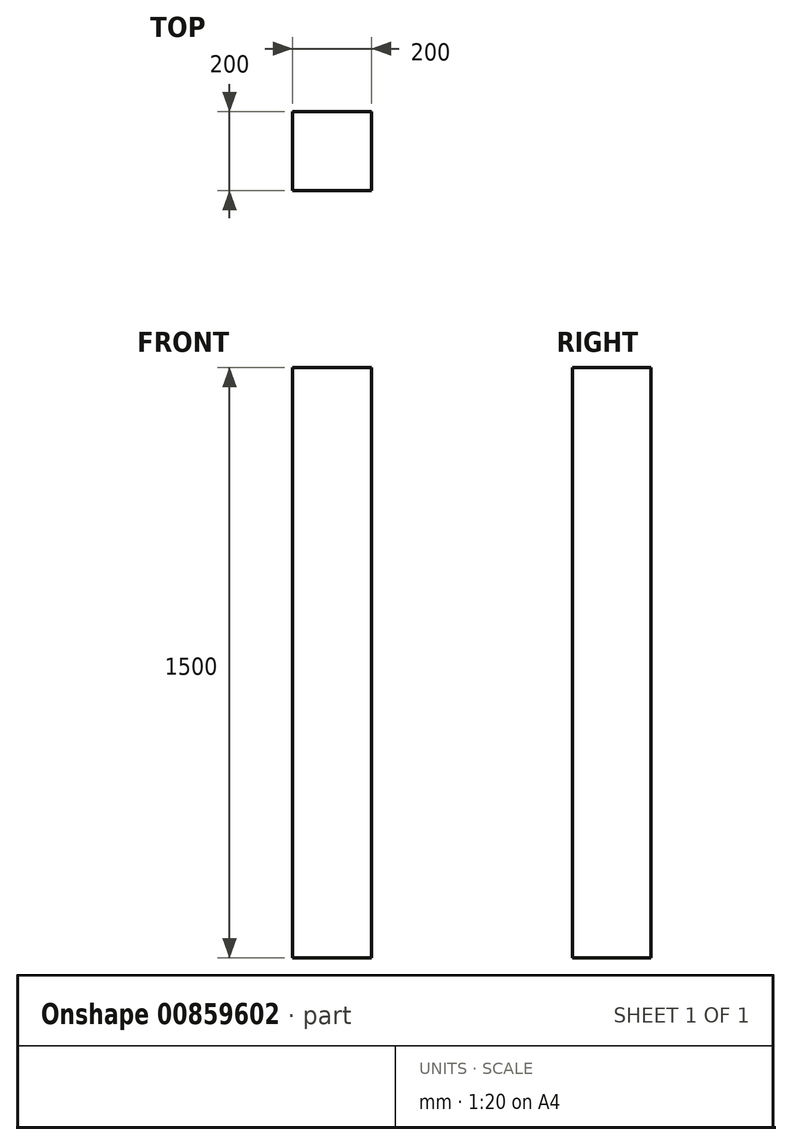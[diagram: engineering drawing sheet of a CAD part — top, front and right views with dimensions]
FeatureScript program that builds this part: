
annotation { "Feature Type Name" : "Feature", "Feature Type Description" : "" }
export const myFeature = defineFeature(function(context is Context, id is Id, definition is map)
    precondition{}
    {
        {
            var Q0;
            Q0=qCreatedBy(makeId("Top.planeOp"),FACE);
            var sketch = newSketch(context, id + "F0", { "sketchPlane" : qUnion([Q0])});
            skLineSegment(sketch, "E0.bottom", {"start": v(-113.92, 101.97) * mm, "end": v(86.08, 101.97) * mm});
            skLineSegment(sketch, "E0.top", {"start": v(-113.92, -98.03) * mm, "end": v(86.08, -98.03) * mm});
            skLineSegment(sketch, "E0.left", {"start": v(-113.92, 101.97) * mm, "end": v(-113.92, -98.03) * mm});
            skLineSegment(sketch, "E0.right", {"start": v(86.08, 101.97) * mm, "end": v(86.08, -98.03) * mm});
            skSolve(sketch);
        }
        {
            var Q0;
            Q0 = qSketchRegion(id + "F0", true);
            extrude(context, id + "F1", {"entities" : qUnion([Q0]), "depth" : 1500 * mm, "offsetDistance" : 25.4 * mm});
        }
    });
